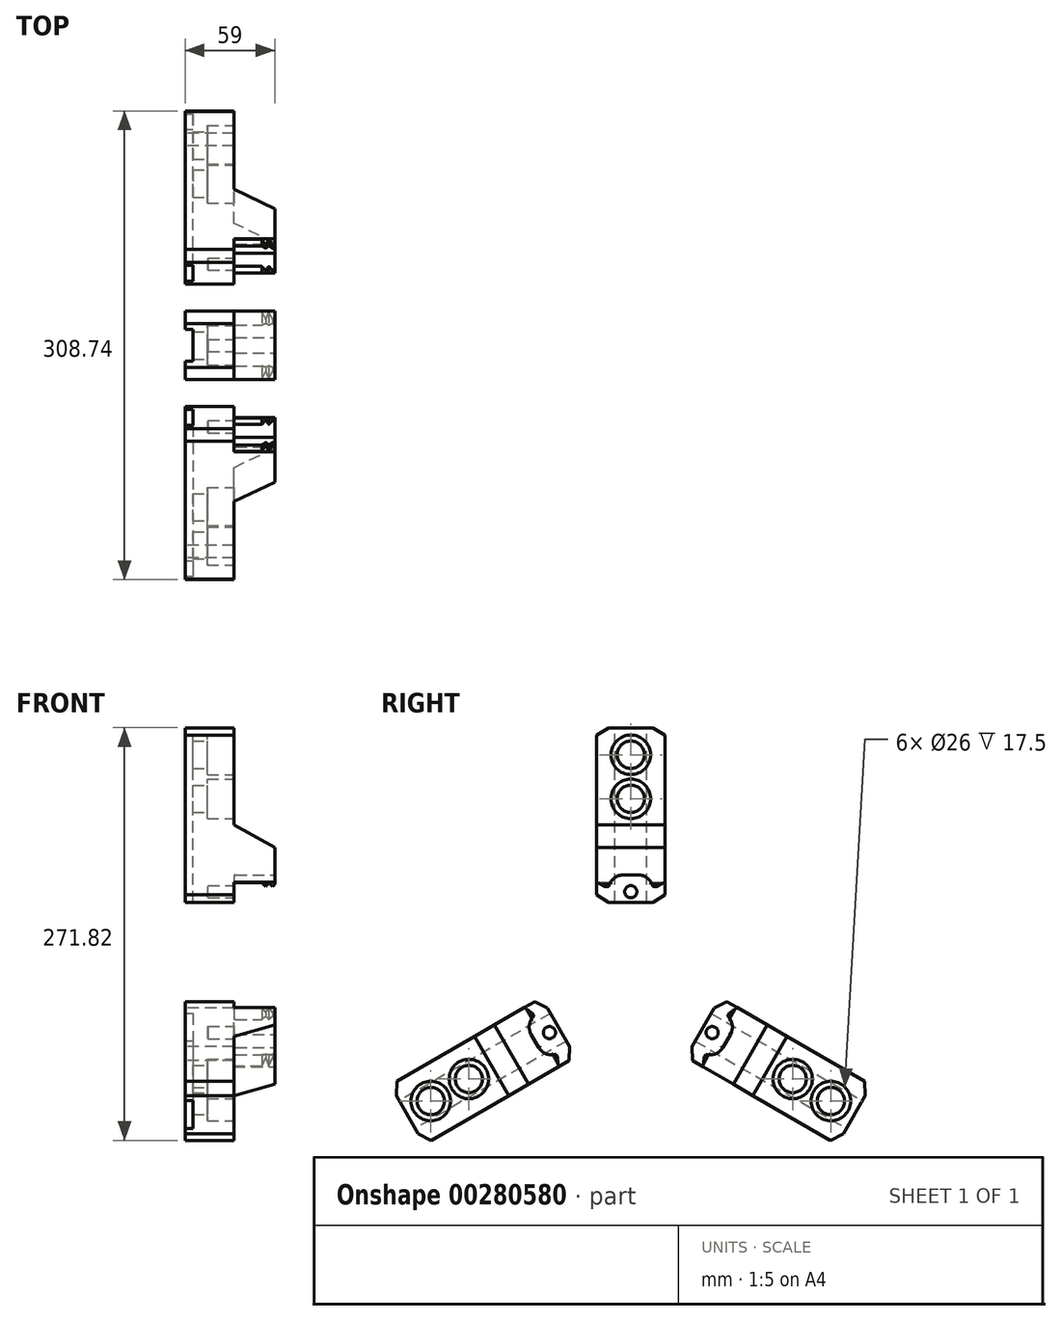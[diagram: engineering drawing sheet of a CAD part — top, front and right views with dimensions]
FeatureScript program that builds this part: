
annotation { "Feature Type Name" : "Feature", "Feature Type Description" : "" }
export const myFeature = defineFeature(function(context is Context, id is Id, definition is map)
    precondition{}
    {
        {
            var Q0;
            Q0=qCreatedBy(makeId("Right.planeOp"),FACE);
            var sketch = newSketch(context, id + "F0", { "sketchPlane" : qUnion([Q0])});
            skLineSegment(sketch, "E0", {"start": v(0, 0) * mm, "end": v(0, 186.29) * mm, "construction": true});
            skLineSegment(sketch, "E1", {"start": v(0, 54.89) * mm, "end": v(14.5, 54.89) * mm});
            skLineSegment(sketch, "E2", {"start": v(14.5, 54.89) * mm, "end": v(22.5, 59.89) * mm});
            skLineSegment(sketch, "E3", {"start": v(22.5, 59.89) * mm, "end": v(22.5, 164.88) * mm});
            skLineSegment(sketch, "E4", {"start": v(22.5, 164.88) * mm, "end": v(14.5, 169.89) * mm});
            skLineSegment(sketch, "E5", {"start": v(14.5, 169.89) * mm, "end": v(0, 169.89) * mm});
            skLineSegment(sketch, "E6", {"start": v(0, 169.89) * mm, "end": v(-14.5, 169.89) * mm});
            skLineSegment(sketch, "E7", {"start": v(-14.5, 169.89) * mm, "end": v(-22.5, 164.88) * mm});
            skLineSegment(sketch, "E8", {"start": v(-22.5, 164.88) * mm, "end": v(-22.5, 59.89) * mm});
            skLineSegment(sketch, "E9", {"start": v(-22.5, 59.89) * mm, "end": v(-14.5, 54.89) * mm});
            skLineSegment(sketch, "E10", {"start": v(-14.5, 54.89) * mm, "end": v(0, 54.89) * mm});
            skLineSegment(sketch, "E11", {"start": v(0, 65.39) * mm, "end": v(-26.74, 65.39) * mm, "construction": true});
            skLineSegment(sketch, "E12", {"start": v(0, 65.39) * mm, "end": v(26.44, 65.39) * mm, "construction": true});
            skCircle(sketch, "E13", {"center": v(0, 0) * mm, "radius": 65.39 * mm, "construction": true});
            skSolve(sketch);
        }
        {
            var Q0;
            Q0 = qSketchRegion(id + "F0", true);
            var Q1;
            Q1=makeQuery(id+"F0.imprint","IMPRINT",FACE,{"disambiguationData":[TD([[makeQuery(id+"F0.imprint","IMPRINT",EDGE,{"derivedFrom":sQuery(id+"F0.wireOp",EDGE,"E1")}),1.0]])]});
            extrude(context, id + "F1", {"entities" : qUnion([Q0, Q1]), "depth" : 62 * mm, "hasSecondDirection" : true, "secondDirectionOppositeDirection" : false, "secondDirectionDepth" : 3 * mm});
        }
        {
            var Q0;
            Q0=makeQuery(id+"F1.opExtrude","SWEPT_FACE",FACE,{"disambiguationData":[OSD([sQuery(id+"F0.wireOp",EDGE,"E8")])]});
            var sketch = newSketch(context, id + "F2", { "sketchPlane" : qUnion([Q0])});
            skLineSegment(sketch, "E14", {"start": v(35, 169.89) * mm, "end": v(35, 105.89) * mm});
            skLineSegment(sketch, "E15", {"start": v(35, 105.88) * mm, "end": v(62, 90.88) * mm});
            skLineSegment(sketch, "E16", {"start": v(53.5, 67.89) * mm, "end": v(35, 67.89) * mm});
            skLineSegment(sketch, "E17", {"start": v(35, 67.89) * mm, "end": v(35, 54.89) * mm});
            skLineSegment(sketch, "E18", {"start": v(51.34, 65.39) * mm, "end": v(69.23, 65.39) * mm, "construction": true});
            skLineSegment(sketch, "E19", {"start": v(53.5, 67.89) * mm, "end": v(56, 65.39) * mm});
            skLineSegment(sketch, "E20", {"start": v(56, 65.39) * mm, "end": v(58, 67.89) * mm});
            skLineSegment(sketch, "E21", {"start": v(58, 67.89) * mm, "end": v(60.5, 65.39) * mm});
            skLineSegment(sketch, "E22", {"start": v(60.5, 65.39) * mm, "end": v(62, 66.89) * mm});
            skLineSegment(sketch, "E23", {"start": v(62, 66.89) * mm, "end": v(62, 67.89) * mm});
            skLineSegment(sketch, "E24", {"start": v(62, 90.89) * mm, "end": v(62, 169.89) * mm});
            skLineSegment(sketch, "E25", {"start": v(62, 169.89) * mm, "end": v(35, 169.89) * mm});
            skLineSegment(sketch, "E26", {"start": v(35, 54.89) * mm, "end": v(62, 54.89) * mm});
            skLineSegment(sketch, "E27", {"start": v(62, 54.89) * mm, "end": v(62, 66.89) * mm});
            skSolve(sketch);
        }
        {
            var Q0;
            {var subQ0=sQuery(id+"F2.wireOp",EDGE,"E25");Q0=makeQuery(id+"F2.imprint","IMPRINT",FACE,{"disambiguationData":[TD([[makeQuery(id+"F2.imprint","IMPRINT",EDGE,{"derivedFrom":subQ0}),1.0]])]});}
            var Q1;
            {var subQ0=sQuery(id+"F2.wireOp",EDGE,"E26");Q1=makeQuery(id+"F2.imprint","IMPRINT",FACE,{"disambiguationData":[TD([[makeQuery(id+"F2.imprint","IMPRINT",EDGE,{"derivedFrom":subQ0}),1.0]])]});}
            var Q2;
            {var subQ0=sQuery(id+"F2.wireOp",EDGE,"E15");Q2=makeQuery(id+"F2.imprint","IMPRINT",FACE,{"disambiguationData":[TD([[makeQuery(id+"F2.imprint","IMPRINT",EDGE,{"derivedFrom":subQ0}),1.0]])]});}
            var Q3;
            {var subQ1=sQuery(id+"F2.wireOp",EDGE,"E16");Q3=makeQuery(id+"F2.imprint","IMPRINT",FACE,{"disambiguationData":[TD([[makeQuery(id+"F2.imprint","IMPRINT",EDGE,{"derivedFrom":subQ1}),1.0]])]});}
            var Q4;
            Q4=makeQuery(id+"F1.opExtrude","SWEPT_FACE",FACE,{"disambiguationData":[OSD([sQuery(id+"F0.wireOp",EDGE,"E3")])]});
            extrude(context, id + "F3", {"entities" : qUnion([Q0, Q1, Q2, Q3]), "operationType" : NewBodyOperationType.REMOVE, "endBound" : BoundingType.UP_TO_SURFACE, "oppositeDirection" : true, "endBoundEntityFace" : qUnion([Q4]), "depth" : 25 * mm});
        }
        {
            var Q0;
            Q0=makeQuery(id+"F1.opExtrude","CAP_FACE",FACE,{"disambiguationData":[OSD([sQuery(id+"F0.wireOp",EDGE,"E1"),sQuery(id+"F0.wireOp",EDGE,"E2"),sQuery(id+"F0.wireOp",EDGE,"E3"),sQuery(id+"F0.wireOp",EDGE,"E4"),sQuery(id+"F0.wireOp",EDGE,"E5"),sQuery(id+"F0.wireOp",EDGE,"E6"),sQuery(id+"F0.wireOp",EDGE,"E7"),sQuery(id+"F0.wireOp",EDGE,"E8"),sQuery(id+"F0.wireOp",EDGE,"E9"),sQuery(id+"F0.wireOp",EDGE,"E10")])],"isStart":false});
            var sketch = newSketch(context, id + "F4", { "sketchPlane" : qUnion([Q0])});
            skLineSegment(sketch, "E28", {"start": v(0, 0) * mm, "end": v(0, 148.13) * mm, "construction": true});
            skPoint(sketch, "E28.endSnap0", {"position": v(0, 90.89) * mm});
            skLineSegment(sketch, "E29", {"start": v(14.5, 65.39) * mm, "end": v(17, 65.39) * mm});
            skLineSegment(sketch, "E30", {"start": v(17, 65.39) * mm, "end": v(22.5, 68.09) * mm});
            skPoint(sketch, "E31", {"position": v(5, 72.89) * mm});
            skArc(sketch, "E32", {"start": v(14.5, 65.39) * mm, "mid": v(11.01, 70.74) * mm, "end": v(5, 72.88) * mm});
            skPoint(sketch, "E32.third.point", {"position": v(11.41, 70.4) * mm});
            skLineSegment(sketch, "E33", {"start": v(22.5, 68.09) * mm, "end": v(22.5, 65.39) * mm});
            skLineSegment(sketch, "E34", {"start": v(22.5, 65.39) * mm, "end": v(17, 65.39) * mm});
            skLineSegment(sketch, "E35", {"start": v(0, 72.89) * mm, "end": v(5, 72.89) * mm});
            skLineSegment(sketch, "E36", {"start": v(14.5, 65.39) * mm, "end": v(0, 65.39) * mm});
            skLineSegment(sketch, "E37", {"start": v(0, 65.39) * mm, "end": v(0, 72.89) * mm});
            skLineSegment(sketch, "E38.MirrorCS", {"start": v(0, 72.89) * mm, "end": v(-5, 72.89) * mm});
            skArc(sketch, "E39.MirrorCS", {"start": v(-14.5, 65.39) * mm, "mid": v(-11.01, 70.74) * mm, "end": v(-5, 72.88) * mm});
            skLineSegment(sketch, "E40.MirrorCS", {"start": v(-14.5, 65.39) * mm, "end": v(-17, 65.39) * mm});
            skLineSegment(sketch, "E41.MirrorCS", {"start": v(-17, 65.39) * mm, "end": v(-22.5, 68.09) * mm});
            skLineSegment(sketch, "E42.MirrorCS", {"start": v(-22.5, 68.09) * mm, "end": v(-22.5, 65.39) * mm});
            skLineSegment(sketch, "E43.MirrorCS", {"start": v(-22.5, 65.39) * mm, "end": v(-17, 65.39) * mm});
            skLineSegment(sketch, "E44.MirrorCS", {"start": v(-14.5, 65.39) * mm, "end": v(0, 65.39) * mm});
            skSolve(sketch);
        }
        {
            var Q0;
            Q0 = qSketchRegion(id + "F4", true);
            var Q1;
            Q1=makeQuery(id+"F3.boolean.opBoolean","COPY",FACE,{"derivedFrom":makeQuery(id+"F3.opExtrude","SWEPT_FACE",FACE,{"disambiguationData":[OSD([sQuery(id+"F2.wireOp",EDGE,"E17")])]})});
            extrude(context, id + "F5", {"entities" : qUnion([Q0]), "operationType" : NewBodyOperationType.REMOVE, "endBound" : BoundingType.UP_TO_SURFACE, "oppositeDirection" : true, "endBoundEntityFace" : qUnion([Q1]), "depth" : 25 * mm});
        }
        {
            var Q0;
            Q0=makeQuery(id+"F5.boolean.opBoolean","MERGE",FACE,{"derivedFrom":[makeQuery(id+"F3.boolean.opBoolean","COPY",FACE,{"derivedFrom":makeQuery(id+"F3.opExtrude","SWEPT_FACE",FACE,{"disambiguationData":[OSD([sQuery(id+"F2.wireOp",EDGE,"E17")])]})})],"fromTools":[makeQuery(id+"F5.opExtrude","CAP_FACE",FACE,{"disambiguationData":[OSD([sQuery(id+"F4.wireOp",EDGE,"E30"),sQuery(id+"F4.wireOp",EDGE,"E33"),sQuery(id+"F4.wireOp",EDGE,"E34")])],"isStart":false}),makeQuery(id+"F5.opExtrude","CAP_FACE",FACE,{"disambiguationData":[OSD([sQuery(id+"F4.wireOp",EDGE,"E32"),sQuery(id+"F4.wireOp",EDGE,"E35"),sQuery(id+"F4.wireOp",EDGE,"E36"),sQuery(id+"F4.wireOp",EDGE,"E38.MirrorCS"),sQuery(id+"F4.wireOp",EDGE,"E39.MirrorCS"),sQuery(id+"F4.wireOp",EDGE,"E44.MirrorCS")])],"isStart":false}),makeQuery(id+"F5.opExtrude","CAP_FACE",FACE,{"disambiguationData":[OSD([sQuery(id+"F4.wireOp",EDGE,"E41.MirrorCS"),sQuery(id+"F4.wireOp",EDGE,"E42.MirrorCS"),sQuery(id+"F4.wireOp",EDGE,"E43.MirrorCS")])],"isStart":false})]});
            var sketch = newSketch(context, id + "F6", { "sketchPlane" : qUnion([Q0])});
            skCircle(sketch, "E45", {"center": v(0, 61.89) * mm, "radius": 4 * mm});
            skSolve(sketch);
        }
        {
            var Q0;
            Q0 = qSketchRegion(id + "F6", true);
            extrude(context, id + "F7", {"entities" : qUnion([Q0]), "operationType" : NewBodyOperationType.REMOVE, "oppositeDirection" : true, "depth" : 17 * mm});
        }
        {
            var Q0;
            {var subQ0=sQuery(id+"F4.wireOp",EDGE,"E30");var subQ1=sQuery(id+"F2.wireOp",EDGE,"E17");var subQ2=sQuery(id+"F2.wireOp",EDGE,"E16");Q0=makeQuery(id+"F5.boolean.opBoolean","SPLIT",EDGE,{"disambiguationData":[TD([makeQuery(id+"F5.opExtrude","SWEPT_FACE",FACE,{"disambiguationData":[OSD([subQ0])]})])],"derivedFrom":makeQuery(id+"F3.boolean.opBoolean","COPY",EDGE,{"derivedFrom":makeQuery(id+"F3.opExtrude","SWEPT_EDGE",EDGE,{"disambiguationData":[OSD([subQ2,subQ1])]})})});}
            var Q1;
            Q1=makeQuery(id+"F5.boolean.opBoolean","COPY",EDGE,{"derivedFrom":makeQuery(id+"F5.opExtrude","CAP_EDGE",EDGE,{"disambiguationData":[OSD([sQuery(id+"F4.wireOp",EDGE,"E32")])],"isStart":false})});
            var Q2;
            Q2=makeQuery(id+"F5.boolean.opBoolean","COPY",EDGE,{"derivedFrom":makeQuery(id+"F5.opExtrude","CAP_EDGE",EDGE,{"disambiguationData":[OSD([sQuery(id+"F4.wireOp",EDGE,"E35"),sQuery(id+"F4.wireOp",EDGE,"E38.MirrorCS")])],"isStart":false})});
            var Q3;
            Q3=makeQuery(id+"F5.boolean.opBoolean","COPY",EDGE,{"derivedFrom":makeQuery(id+"F5.opExtrude","CAP_EDGE",EDGE,{"disambiguationData":[OSD([sQuery(id+"F4.wireOp",EDGE,"E39.MirrorCS")])],"isStart":false})});
            var Q4;
            {var subQ0=sQuery(id+"F2.wireOp",EDGE,"E17");var subQ2=sQuery(id+"F4.wireOp",EDGE,"E39.MirrorCS");var subQ3=sQuery(id+"F2.wireOp",EDGE,"E16");Q4=makeQuery(id+"F5.boolean.opBoolean","SPLIT",EDGE,{"disambiguationData":[TD([makeQuery(id+"F5.opExtrude","SWEPT_FACE",FACE,{"disambiguationData":[OSD([subQ2])]})])],"derivedFrom":makeQuery(id+"F3.boolean.opBoolean","COPY",EDGE,{"derivedFrom":makeQuery(id+"F3.opExtrude","SWEPT_EDGE",EDGE,{"disambiguationData":[OSD([subQ3,subQ0])]})})});}
            fillet(context, id + "F8", {"entities" : qUnion([Q0, Q1, Q2, Q3, Q4]), "radius" : 1 * mm, "tangentPropagation" : true, "allowEdgeOverflow" : false});
        }
        {
            var Q0;
            Q0=makeQuery(id+"F3.boolean.opBoolean","COPY",FACE,{"derivedFrom":makeQuery(id+"F3.opExtrude","SWEPT_FACE",FACE,{"disambiguationData":[OSD([sQuery(id+"F2.wireOp",EDGE,"E14")])]})});
            var sketch = newSketch(context, id + "F9", { "sketchPlane" : qUnion([Q0])});
            skCircle(sketch, "E46", {"center": v(0, 152.09) * mm, "radius": 13 * mm});
            skCircle(sketch, "E47", {"center": v(0, 123.08) * mm, "radius": 13 * mm});
            skCircle(sketch, "E48", {"center": v(0, 152.09) * mm, "radius": 9 * mm});
            skCircle(sketch, "E49", {"center": v(0, 123.08) * mm, "radius": 9 * mm});
            skSolve(sketch);
        }
        {
            var Q0;
            Q0=makeQuery(id+"F9.imprint","IMPRINT",FACE,{"disambiguationData":[TD([[makeQuery(id+"F9.imprint","IMPRINT",EDGE,{"derivedFrom":sQuery(id+"F9.wireOp",EDGE,"E48")}),1.0]])]});
            var Q1;
            Q1=makeQuery(id+"F9.imprint","IMPRINT",FACE,{"disambiguationData":[TD([[makeQuery(id+"F9.imprint","IMPRINT",EDGE,{"derivedFrom":sQuery(id+"F9.wireOp",EDGE,"E49")}),1.0]])]});
            var Q2;
            Q2=makeQuery(id+"F1.opExtrude","CAP_FACE",FACE,{"disambiguationData":[OSD([sQuery(id+"F0.wireOp",EDGE,"E1"),sQuery(id+"F0.wireOp",EDGE,"E2"),sQuery(id+"F0.wireOp",EDGE,"E3"),sQuery(id+"F0.wireOp",EDGE,"E4"),sQuery(id+"F0.wireOp",EDGE,"E5"),sQuery(id+"F0.wireOp",EDGE,"E6"),sQuery(id+"F0.wireOp",EDGE,"E7"),sQuery(id+"F0.wireOp",EDGE,"E8"),sQuery(id+"F0.wireOp",EDGE,"E9"),sQuery(id+"F0.wireOp",EDGE,"E10")])],"isStart":true});
            extrude(context, id + "F10", {"entities" : qUnion([Q0, Q1]), "operationType" : NewBodyOperationType.REMOVE, "endBound" : BoundingType.UP_TO_SURFACE, "oppositeDirection" : true, "endBoundEntityFace" : qUnion([Q2]), "depth" : 25 * mm});
        }
        {
            var Q0;
            Q0=makeQuery(id+"F9.imprint","IMPRINT",FACE,{"disambiguationData":[TD([[makeQuery(id+"F9.imprint","IMPRINT",EDGE,{"derivedFrom":sQuery(id+"F9.wireOp",EDGE,"E46")}),1.0]])]});
            var Q1;
            Q1=makeQuery(id+"F9.imprint","IMPRINT",FACE,{"disambiguationData":[TD([[makeQuery(id+"F9.imprint","IMPRINT",EDGE,{"derivedFrom":sQuery(id+"F9.wireOp",EDGE,"E47")}),1.0]])]});
            extrude(context, id + "F11", {"entities" : qUnion([Q0, Q1]), "operationType" : NewBodyOperationType.REMOVE, "oppositeDirection" : true, "depth" : 17.5 * mm});
        }
        {
            var Q0;
            Q0=makeQuery(id+"F1.opExtrude","SWEPT_FACE",FACE,{"disambiguationData":[OSD([sQuery(id+"F0.wireOp",EDGE,"E5"),sQuery(id+"F0.wireOp",EDGE,"E6")])]});
            var sketch = newSketch(context, id + "F12", { "sketchPlane" : qUnion([Q0])});
            skLineSegment(sketch, "E50", {"start": v(3, 0) * mm, "end": v(3, -10.5) * mm});
            skLineSegment(sketch, "E51", {"start": v(3, -10.5) * mm, "end": v(8, -10.5) * mm});
            skLineSegment(sketch, "E52", {"start": v(8, -10.5) * mm, "end": v(8, 0) * mm});
            skLineSegment(sketch, "E53", {"start": v(8, 0) * mm, "end": v(8, 10.5) * mm});
            skLineSegment(sketch, "E54", {"start": v(8, 10.5) * mm, "end": v(3, 10.5) * mm});
            skLineSegment(sketch, "E55", {"start": v(3, 10.5) * mm, "end": v(3, 0) * mm});
            skSolve(sketch);
        }
        {
            var Q0;
            Q0=makeQuery(id+"F12.imprint","IMPRINT",FACE,{"disambiguationData":[TD([[makeQuery(id+"F12.imprint","IMPRINT",EDGE,{"derivedFrom":sQuery(id+"F12.wireOp",EDGE,"E50")}),1.0]])]});
            var Q1;
            Q1=makeQuery(id+"F1.opExtrude","SWEPT_FACE",FACE,{"disambiguationData":[OSD([sQuery(id+"F0.wireOp",EDGE,"E1"),sQuery(id+"F0.wireOp",EDGE,"E10")])]});
            extrude(context, id + "F13", {"entities" : qUnion([Q0]), "operationType" : NewBodyOperationType.REMOVE, "endBound" : BoundingType.UP_TO_SURFACE, "oppositeDirection" : true, "endBoundEntityFace" : qUnion([Q1]), "depth" : 25 * mm});
        }
        {
            var Q0;
            Q0=qCreatedBy(makeId("Front.planeOp"),FACE);
            var sketch = newSketch(context, id + "F14", { "sketchPlane" : qUnion([Q0])});
            skLineSegment(sketch, "E56", {"start": v(0, 0) * mm, "end": v(70.74, 0) * mm, "construction": true});
            skSolve(sketch);
        }
        {
            var Q0;
            Q0=makeQuery(id+"F1.opExtrude","SWEPT_BODY",BODY,{"disambiguationData":[OSD([sQuery(id+"F0.wireOp",EDGE,"E1"),sQuery(id+"F0.wireOp",EDGE,"E2"),sQuery(id+"F0.wireOp",EDGE,"E3"),sQuery(id+"F0.wireOp",EDGE,"E4"),sQuery(id+"F0.wireOp",EDGE,"E5"),sQuery(id+"F0.wireOp",EDGE,"E6"),sQuery(id+"F0.wireOp",EDGE,"E7"),sQuery(id+"F0.wireOp",EDGE,"E8"),sQuery(id+"F0.wireOp",EDGE,"E9"),sQuery(id+"F0.wireOp",EDGE,"E10")])]});
            var Q1;
            Q1=sQuery(id+"F14.wireOp",EDGE,"E56");
            circularPattern(context, id + "F15", {"entities" : qUnion([Q0]), "axis" : qUnion([Q1]), "angle" : 360 * degree, "instanceCount" : 3, "equalSpace" : true, "computeTransformsWithoutBuiltin" : true});
        }
    });
